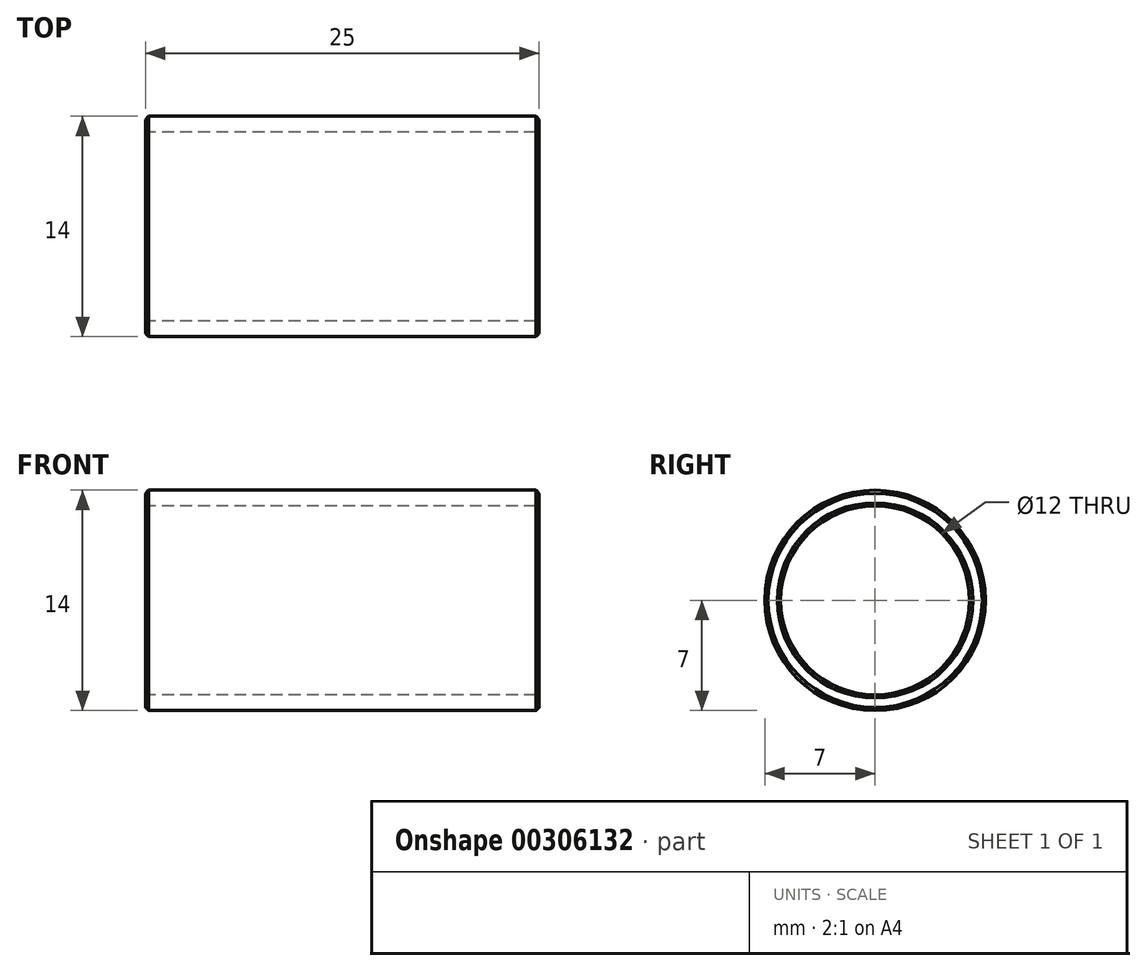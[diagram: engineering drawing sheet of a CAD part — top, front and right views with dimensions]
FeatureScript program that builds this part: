
annotation { "Feature Type Name" : "Feature", "Feature Type Description" : "" }
export const myFeature = defineFeature(function(context is Context, id is Id, definition is map)
    precondition{}
    {
        {
            var Q0;
            Q0=qCreatedBy(makeId("Right.planeOp"),FACE);
            var sketch = newSketch(context, id + "F0", { "sketchPlane" : qUnion([Q0])});
            skCircle(sketch, "E0", {"center": v(0, 0) * mm, "radius": 6 * mm});
            skCircle(sketch, "E1", {"center": v(0, 0) * mm, "radius": 7 * mm});
            skSolve(sketch);
        }
        {
            var Q0;
            Q0=makeQuery(id+"F0.imprint","IMPRINT",FACE,{"disambiguationData":[TD([[makeQuery(id+"F0.imprint","IMPRINT",EDGE,{"derivedFrom":sQuery(id+"F0.wireOp",EDGE,"E0")}),-1.0]])]});
            extrude(context, id + "F1", {"entities" : qUnion([Q0]), "depth" : 25 * mm});
        }
        {
            var Q0;
            Q0=makeQuery(id+"F1.opExtrude","CAP_EDGE",EDGE,{"disambiguationData":[OSD([sQuery(id+"F0.wireOp",EDGE,"E1")])],"isStart":true});
            var Q1;
            Q1=makeQuery(id+"F1.opExtrude","CAP_EDGE",EDGE,{"disambiguationData":[OSD([sQuery(id+"F0.wireOp",EDGE,"E1")])],"isStart":false});
            var Q2;
            Q2=makeQuery(id+"F1.opExtrude","CAP_EDGE",EDGE,{"disambiguationData":[OSD([sQuery(id+"F0.wireOp",EDGE,"E0")])],"isStart":false});
            var Q3;
            Q3=makeQuery(id+"F1.opExtrude","CAP_EDGE",EDGE,{"disambiguationData":[OSD([sQuery(id+"F0.wireOp",EDGE,"E0")])],"isStart":true});
            chamfer(context, id + "F2", {"entities" : qUnion([Q0, Q1, Q2, Q3]), "width" : 0.2 * mm, "tangentPropagation" : true});
        }
    });
